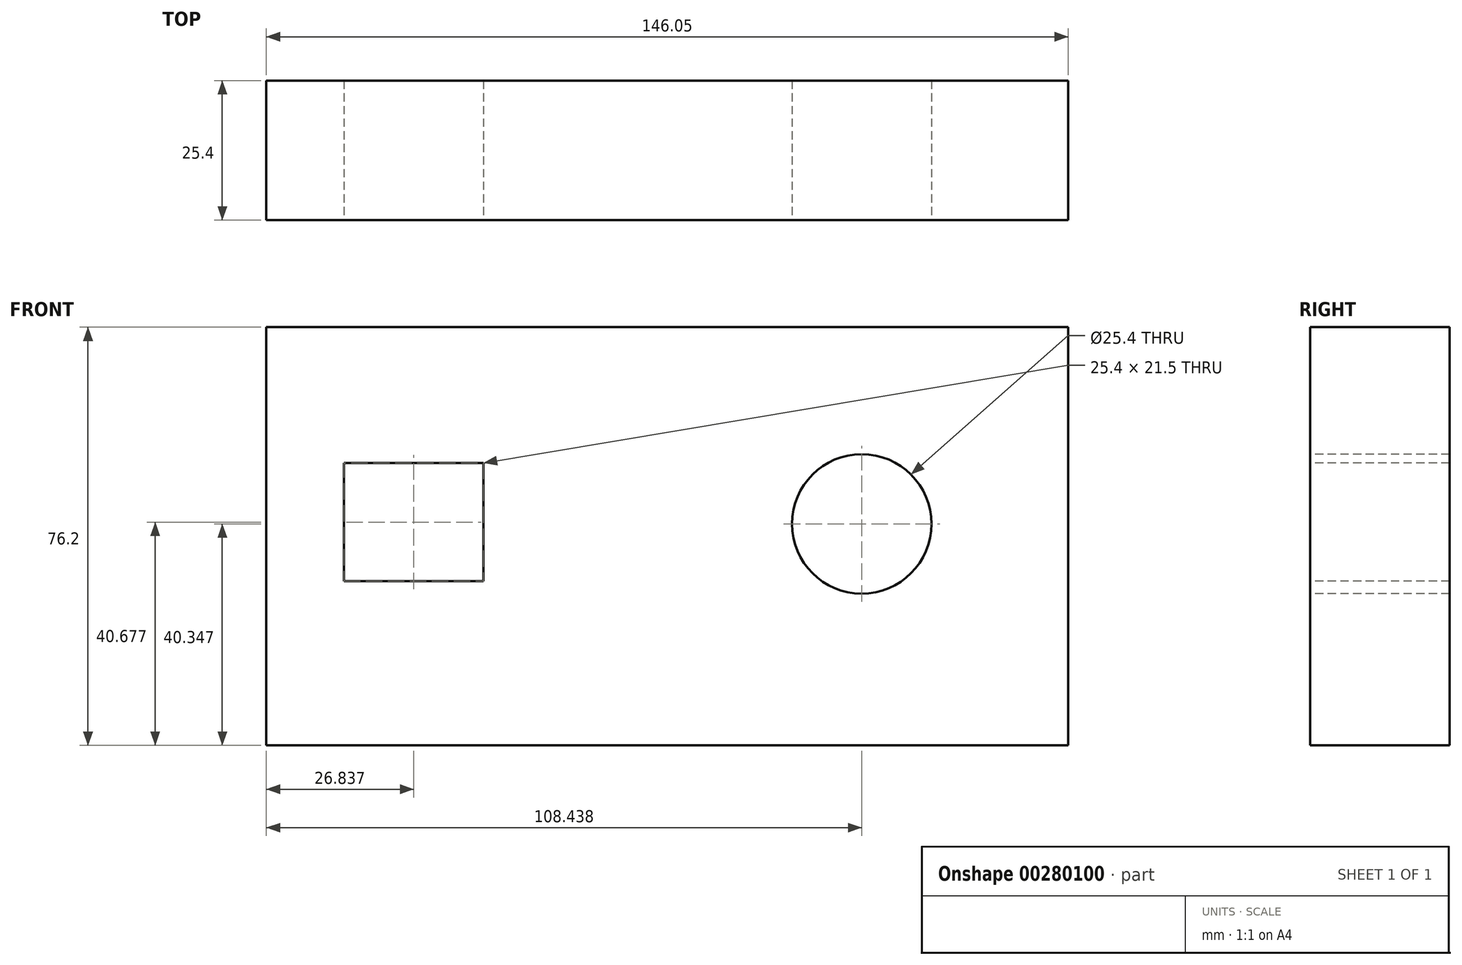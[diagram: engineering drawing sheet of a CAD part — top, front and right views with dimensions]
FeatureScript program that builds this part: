
annotation { "Feature Type Name" : "Feature", "Feature Type Description" : "" }
export const myFeature = defineFeature(function(context is Context, id is Id, definition is map)
    precondition{}
    {
        {
            var Q0;
            Q0=qCreatedBy(makeId("Front.planeOp"),FACE);
            var sketch = newSketch(context, id + "F0", { "sketchPlane" : qUnion([Q0])});
            skLineSegment(sketch, "E0", {"start": v(97.55, 2.67) * mm, "end": v(97.55, 78.87) * mm});
            skLineSegment(sketch, "E1", {"start": v(97.55, 78.87) * mm, "end": v(-48.5, 78.87) * mm});
            skLineSegment(sketch, "E2", {"start": v(-48.5, 78.87) * mm, "end": v(-48.5, 2.67) * mm});
            skLineSegment(sketch, "E3", {"start": v(-48.5, 2.67) * mm, "end": v(97.55, 2.67) * mm});
            skSolve(sketch);
        }
        {
            var Q0;
            Q0=makeQuery(id+"F0.imprint","IMPRINT",FACE,{"disambiguationData":[TD([[makeQuery(id+"F0.imprint","IMPRINT",EDGE,{"derivedFrom":sQuery(id+"F0.wireOp",EDGE,"E0")}),1.0]])]});
            extrude(context, id + "F1", {"entities" : qUnion([Q0]), "depth" : 25.4 * mm});
        }
        {
            var Q0;
            Q0=makeQuery(id+"F1.opExtrude","CAP_FACE",FACE,{"disambiguationData":[OSD([sQuery(id+"F0.wireOp",EDGE,"E0"),sQuery(id+"F0.wireOp",EDGE,"E1"),sQuery(id+"F0.wireOp",EDGE,"E2"),sQuery(id+"F0.wireOp",EDGE,"E3")])],"isStart":false});
            var sketch = newSketch(context, id + "F2", { "sketchPlane" : qUnion([Q0])});
            skCircle(sketch, "E4", {"center": v(59.94, 43.02) * mm, "radius": 12.7 * mm});
            skLineSegment(sketch, "E5.bottom", {"start": v(-34.36, 54.1) * mm, "end": v(-8.96, 54.1) * mm});
            skLineSegment(sketch, "E5.top", {"start": v(-34.36, 32.6) * mm, "end": v(-8.96, 32.6) * mm});
            skLineSegment(sketch, "E5.left", {"start": v(-34.36, 54.1) * mm, "end": v(-34.36, 32.6) * mm});
            skLineSegment(sketch, "E5.right", {"start": v(-8.96, 54.1) * mm, "end": v(-8.96, 32.6) * mm});
            skSolve(sketch);
        }
        {
            var Q0;
            Q0 = qSketchRegion(id + "F2", true);
            extrude(context, id + "F3", {"entities" : qUnion([Q0]), "operationType" : NewBodyOperationType.REMOVE, "oppositeDirection" : true, "depth" : 1105.4 * mm});
        }
    });
